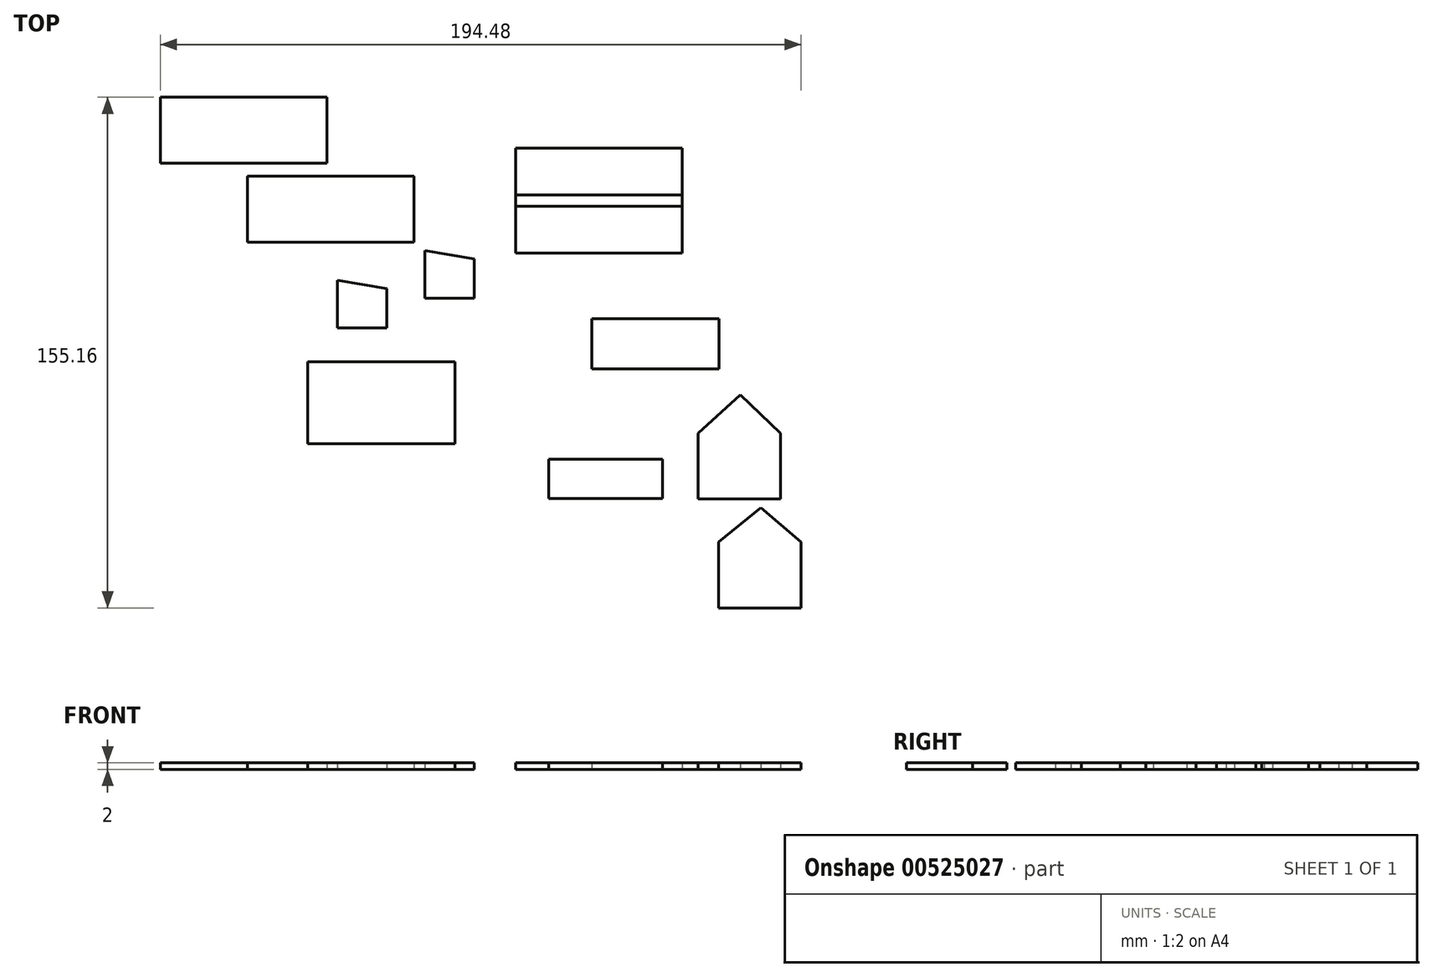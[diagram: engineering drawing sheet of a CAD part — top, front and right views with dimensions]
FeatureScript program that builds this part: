
annotation { "Feature Type Name" : "Feature", "Feature Type Description" : "" }
export const myFeature = defineFeature(function(context is Context, id is Id, definition is map)
    precondition{}
    {
        {
            var Q0;
            Q0=qCreatedBy(makeId("Top.planeOp"),FACE);
            var sketch = newSketch(context, id + "F0", { "sketchPlane" : qUnion([Q0])});
            skLineSegment(sketch, "E0.bottom", {"start": v(-81.4, 49.71) * mm, "end": v(-30.8, 49.71) * mm});
            skLineSegment(sketch, "E0.top", {"start": v(-81.4, 29.71) * mm, "end": v(-30.8, 29.71) * mm});
            skLineSegment(sketch, "E0.left", {"start": v(-81.4, 49.71) * mm, "end": v(-81.4, 29.71) * mm});
            skLineSegment(sketch, "E0.right", {"start": v(-30.8, 49.71) * mm, "end": v(-30.8, 29.71) * mm});
            skSolve(sketch);
        }
        {
            var Q0;
            Q0=qCreatedBy(makeId("Top.planeOp"),FACE);
            var sketch = newSketch(context, id + "F1", { "sketchPlane" : qUnion([Q0])});
            skLineSegment(sketch, "E1.bottom", {"start": v(-107.79, 73.76) * mm, "end": v(-57.2, 73.76) * mm});
            skLineSegment(sketch, "E1.top", {"start": v(-107.79, 53.76) * mm, "end": v(-57.2, 53.76) * mm});
            skLineSegment(sketch, "E1.left", {"start": v(-107.79, 73.76) * mm, "end": v(-107.79, 53.76) * mm});
            skLineSegment(sketch, "E1.right", {"start": v(-57.2, 73.76) * mm, "end": v(-57.2, 53.76) * mm});
            skSolve(sketch);
        }
        {
            var Q0;
            Q0=qCreatedBy(makeId("Top.planeOp"),FACE);
            var sketch = newSketch(context, id + "F2", { "sketchPlane" : qUnion([Q0])});
            skLineSegment(sketch, "E2.bottom", {"start": v(0, 58.32) * mm, "end": v(50.6, 58.32) * mm});
            skLineSegment(sketch, "E2.top", {"start": v(0, 40.64) * mm, "end": v(50.6, 40.64) * mm});
            skLineSegment(sketch, "E2.left", {"start": v(0, 58.32) * mm, "end": v(0, 40.64) * mm});
            skLineSegment(sketch, "E2.right", {"start": v(50.6, 58.32) * mm, "end": v(50.6, 40.64) * mm});
            skSolve(sketch);
        }
        {
            var Q0;
            Q0=qCreatedBy(makeId("Top.planeOp"),FACE);
            var sketch = newSketch(context, id + "F3", { "sketchPlane" : qUnion([Q0])});
            skLineSegment(sketch, "E3.bottom", {"start": v(0, 44.1) * mm, "end": v(50.6, 44.1) * mm});
            skLineSegment(sketch, "E3.top", {"start": v(0, 26.42) * mm, "end": v(50.6, 26.42) * mm});
            skLineSegment(sketch, "E3.left", {"start": v(0, 44.1) * mm, "end": v(0, 26.42) * mm});
            skLineSegment(sketch, "E3.right", {"start": v(50.6, 44.1) * mm, "end": v(50.6, 26.42) * mm});
            skSolve(sketch);
        }
        {
            var Q0;
            Q0=qCreatedBy(makeId("Top.planeOp"),FACE);
            var sketch = newSketch(context, id + "F4", { "sketchPlane" : qUnion([Q0])});
            skLineSegment(sketch, "E4.bottom", {"start": v(-54.1, 15.62) * mm, "end": v(-39.1, 15.62) * mm});
            skLineSegment(sketch, "E4.top", {"start": v(-54.1, 3.62) * mm, "end": v(-39.1, 3.62) * mm});
            skLineSegment(sketch, "E4.left", {"start": v(-54.1, 15.62) * mm, "end": v(-54.1, 3.62) * mm});
            skLineSegment(sketch, "E4.right", {"start": v(-39.1, 15.62) * mm, "end": v(-39.1, 3.62) * mm});
            skPoint(sketch, "E5", {"position": v(-54.1, 18.12) * mm});
            skLineSegment(sketch, "E6", {"start": v(-54.1, 18.12) * mm, "end": v(-39.1, 15.62) * mm});
            skLineSegment(sketch, "E7", {"start": v(-54.1, 18.12) * mm, "end": v(-54.1, 15.62) * mm});
            skSolve(sketch);
        }
        {
            var Q0;
            Q0=qCreatedBy(makeId("Top.planeOp"),FACE);
            var sketch = newSketch(context, id + "F5", { "sketchPlane" : qUnion([Q0])});
            skLineSegment(sketch, "E8.bottom", {"start": v(-27.56, 24.68) * mm, "end": v(-12.56, 24.68) * mm});
            skLineSegment(sketch, "E8.top", {"start": v(-27.56, 12.68) * mm, "end": v(-12.56, 12.68) * mm});
            skLineSegment(sketch, "E8.left", {"start": v(-27.56, 24.68) * mm, "end": v(-27.56, 12.68) * mm});
            skLineSegment(sketch, "E8.right", {"start": v(-12.56, 24.68) * mm, "end": v(-12.56, 12.68) * mm});
            skPoint(sketch, "E9", {"position": v(-27.56, 24.68) * mm});
            skPoint(sketch, "E10", {"position": v(-27.56, 27.18) * mm});
            skLineSegment(sketch, "E11", {"start": v(-27.56, 27.18) * mm, "end": v(-12.56, 24.68) * mm});
            skLineSegment(sketch, "E12", {"start": v(-27.56, 27.18) * mm, "end": v(-27.56, 24.68) * mm});
            skSolve(sketch);
        }
        {
            var Q0;
            Q0=qCreatedBy(makeId("Top.planeOp"),FACE);
            var sketch = newSketch(context, id + "F6", { "sketchPlane" : qUnion([Q0])});
            skLineSegment(sketch, "E13.bottom", {"start": v(23.14, 6.43) * mm, "end": v(61.75, 6.43) * mm});
            skLineSegment(sketch, "E13.top", {"start": v(23.14, -8.78) * mm, "end": v(61.75, -8.78) * mm});
            skLineSegment(sketch, "E13.left", {"start": v(23.14, 6.43) * mm, "end": v(23.14, -8.78) * mm});
            skLineSegment(sketch, "E13.right", {"start": v(61.75, 6.43) * mm, "end": v(61.75, -8.78) * mm});
            skLineSegment(sketch, "E14.bottom", {"start": v(-63.03, -6.55) * mm, "end": v(-18.35, -6.55) * mm});
            skLineSegment(sketch, "E14.top", {"start": v(-63.03, -31.55) * mm, "end": v(-18.35, -31.55) * mm});
            skLineSegment(sketch, "E14.left", {"start": v(-63.03, -6.55) * mm, "end": v(-63.03, -31.55) * mm});
            skLineSegment(sketch, "E14.right", {"start": v(-18.35, -6.55) * mm, "end": v(-18.35, -31.55) * mm});
            skLineSegment(sketch, "E15.bottom", {"start": v(-63.03, -31.55) * mm, "end": v(-29.97, -31.55) * mm});
            skLineSegment(sketch, "E15.top", {"start": v(-58.03, -51.55) * mm, "end": v(-34.97, -51.55) * mm});
            skLineSegment(sketch, "E15.left", {"start": v(-63.03, -31.55) * mm, "end": v(-63.03, -46.55) * mm});
            skLineSegment(sketch, "E15.right", {"start": v(-29.97, -31.55) * mm, "end": v(-29.97, -46.55) * mm});
            skPoint(sketch, "E16.visualSharp", {"position": v(-63.03, -51.55) * mm});
            skArc(sketch, "E16.filletArc", {"start": v(-63.03, -46.55) * mm, "mid": v(-61.57, -50.09) * mm, "end": v(-58.03, -51.55) * mm});
            skPoint(sketch, "E17.visualSharp", {"position": v(-29.97, -51.55) * mm});
            skArc(sketch, "E17.filletArc", {"start": v(-34.97, -51.55) * mm, "mid": v(-31.44, -50.09) * mm, "end": v(-29.97, -46.55) * mm});
            skSolve(sketch);
        }
        {
            var Q0;
            Q0=qCreatedBy(makeId("Top.planeOp"),FACE);
            var sketch = newSketch(context, id + "F7", { "sketchPlane" : qUnion([Q0])});
            skLineSegment(sketch, "E18.bottom", {"start": v(10.06, -36.2) * mm, "end": v(44.67, -36.2) * mm});
            skLineSegment(sketch, "E18.top", {"start": v(10.06, -48.2) * mm, "end": v(44.67, -48.2) * mm});
            skLineSegment(sketch, "E18.left", {"start": v(10.06, -36.2) * mm, "end": v(10.06, -48.2) * mm});
            skLineSegment(sketch, "E18.right", {"start": v(44.67, -36.2) * mm, "end": v(44.67, -48.2) * mm});
            skSolve(sketch);
        }
        {
            var Q0;
            Q0=qCreatedBy(makeId("Top.planeOp"),FACE);
            var sketch = newSketch(context, id + "F8", { "sketchPlane" : qUnion([Q0])});
            skLineSegment(sketch, "E19.bottom", {"start": v(55.47, -28.29) * mm, "end": v(80.47, -28.29) * mm});
            skLineSegment(sketch, "E19.top", {"start": v(55.47, -48.29) * mm, "end": v(80.47, -48.29) * mm});
            skLineSegment(sketch, "E19.left", {"start": v(55.47, -28.29) * mm, "end": v(55.47, -48.29) * mm});
            skLineSegment(sketch, "E19.right", {"start": v(80.47, -28.29) * mm, "end": v(80.47, -48.29) * mm});
            skLineSegment(sketch, "E20", {"start": v(55.47, -28.29) * mm, "end": v(68.24, -16.59) * mm});
            skLineSegment(sketch, "E21", {"start": v(68.24, -16.59) * mm, "end": v(80.47, -28.29) * mm});
            skSolve(sketch);
        }
        {
            var Q0;
            Q0=qCreatedBy(makeId("Top.planeOp"),FACE);
            var sketch = newSketch(context, id + "F9", { "sketchPlane" : qUnion([Q0])});
            skLineSegment(sketch, "E22.bottom", {"start": v(61.69, -61.4) * mm, "end": v(86.69, -61.4) * mm});
            skLineSegment(sketch, "E22.top", {"start": v(61.69, -81.4) * mm, "end": v(86.69, -81.4) * mm});
            skLineSegment(sketch, "E22.left", {"start": v(61.69, -61.4) * mm, "end": v(61.69, -81.4) * mm});
            skLineSegment(sketch, "E22.right", {"start": v(86.69, -61.4) * mm, "end": v(86.69, -81.4) * mm});
            skPoint(sketch, "E23", {"position": v(74.5, -50.96) * mm});
            skLineSegment(sketch, "E24", {"start": v(61.69, -61.4) * mm, "end": v(74.5, -50.96) * mm});
            skLineSegment(sketch, "E25", {"start": v(74.5, -50.96) * mm, "end": v(86.69, -61.4) * mm});
            skSolve(sketch);
        }
        {
            var Q0;
            Q0 = qSketchRegion(id + "F1", true);
            var Q1;
            Q1=makeQuery(id+"F5.imprint","IMPRINT",FACE,{"disambiguationData":[TD([[makeQuery(id+"F5.imprint","IMPRINT",EDGE,{"derivedFrom":sQuery(id+"F5.wireOp",EDGE,"E8.bottom")}),-1.0]])]});
            var Q2;
            Q2=makeQuery(id+"F5.imprint","IMPRINT",FACE,{"disambiguationData":[TD([[makeQuery(id+"F5.imprint","IMPRINT",EDGE,{"derivedFrom":sQuery(id+"F5.wireOp",EDGE,"E8.bottom")}),1.0]])]});
            var Q3;
            Q3=makeQuery(id+"F4.imprint","IMPRINT",FACE,{"disambiguationData":[TD([[makeQuery(id+"F4.imprint","IMPRINT",EDGE,{"derivedFrom":sQuery(id+"F4.wireOp",EDGE,"E4.bottom")}),-1.0]])]});
            var Q4;
            Q4=makeQuery(id+"F4.imprint","IMPRINT",FACE,{"disambiguationData":[TD([[makeQuery(id+"F4.imprint","IMPRINT",EDGE,{"derivedFrom":sQuery(id+"F4.wireOp",EDGE,"E4.bottom")}),1.0]])]});
            var Q5;
            Q5=makeQuery(id+"F0.imprint","IMPRINT",FACE,{"disambiguationData":[TD([[makeQuery(id+"F0.imprint","IMPRINT",EDGE,{"derivedFrom":sQuery(id+"F0.wireOp",EDGE,"E0.bottom")}),-1.0]])]});
            var Q6;
            Q6=makeQuery(id+"F2.imprint","IMPRINT",FACE,{"disambiguationData":[TD([[makeQuery(id+"F2.imprint","IMPRINT",EDGE,{"derivedFrom":sQuery(id+"F2.wireOp",EDGE,"E2.bottom")}),-1.0]])]});
            var Q7;
            Q7=makeQuery(id+"F3.imprint","IMPRINT",FACE,{"disambiguationData":[TD([[makeQuery(id+"F3.imprint","IMPRINT",EDGE,{"derivedFrom":sQuery(id+"F3.wireOp",EDGE,"E3.bottom")}),-1.0]])]});
            var Q8;
            Q8=makeQuery(id+"F6.imprint","IMPRINT",FACE,{"disambiguationData":[TD([[makeQuery(id+"F6.imprint","IMPRINT",EDGE,{"derivedFrom":sQuery(id+"F6.wireOp",EDGE,"E13.bottom")}),-1.0]])]});
            var Q9;
            Q9=makeQuery(id+"F6.imprint","IMPRINT",FACE,{"disambiguationData":[TD([[makeQuery(id+"F6.imprint","IMPRINT",EDGE,{"derivedFrom":sQuery(id+"F6.wireOp",EDGE,"E14.bottom")}),-1.0]])]});
            var Q10;
            Q10=makeQuery(id+"F6.imprint","IMPRINT",FACE,{"disambiguationData":[TD([[makeQuery(id+"F6.imprint","IMPRINT",EDGE,{"derivedFrom":sQuery(id+"F6.wireOp",EDGE,"E15.bottom")}),-1.0]])]});
            var Q11;
            Q11=makeQuery(id+"F7.imprint","IMPRINT",FACE,{"disambiguationData":[TD([[makeQuery(id+"F7.imprint","IMPRINT",EDGE,{"derivedFrom":sQuery(id+"F7.wireOp",EDGE,"E18.bottom")}),-1.0]])]});
            var Q12;
            Q12=makeQuery(id+"F8.imprint","IMPRINT",FACE,{"disambiguationData":[TD([[makeQuery(id+"F8.imprint","IMPRINT",EDGE,{"derivedFrom":sQuery(id+"F8.wireOp",EDGE,"E19.bottom")}),-1.0]])]});
            var Q13;
            Q13=makeQuery(id+"F8.imprint","IMPRINT",FACE,{"disambiguationData":[TD([[makeQuery(id+"F8.imprint","IMPRINT",EDGE,{"derivedFrom":sQuery(id+"F8.wireOp",EDGE,"E19.bottom")}),1.0]])]});
            var Q14;
            Q14=makeQuery(id+"F9.imprint","IMPRINT",FACE,{"disambiguationData":[TD([[makeQuery(id+"F9.imprint","IMPRINT",EDGE,{"derivedFrom":sQuery(id+"F9.wireOp",EDGE,"E22.bottom")}),-1.0]])]});
            var Q15;
            Q15=makeQuery(id+"F9.imprint","IMPRINT",FACE,{"disambiguationData":[TD([[makeQuery(id+"F9.imprint","IMPRINT",EDGE,{"derivedFrom":sQuery(id+"F9.wireOp",EDGE,"E22.bottom")}),1.0]])]});
            extrude(context, id + "F10", {"entities" : qUnion([Q0, Q1, Q2, Q3, Q4, Q5, Q6, Q7, Q8, Q9, Q10, Q11, Q12, Q13, Q14, Q15]), "depth" : 2 * mm, "offsetDistance" : 25 * mm});
        }
    });
